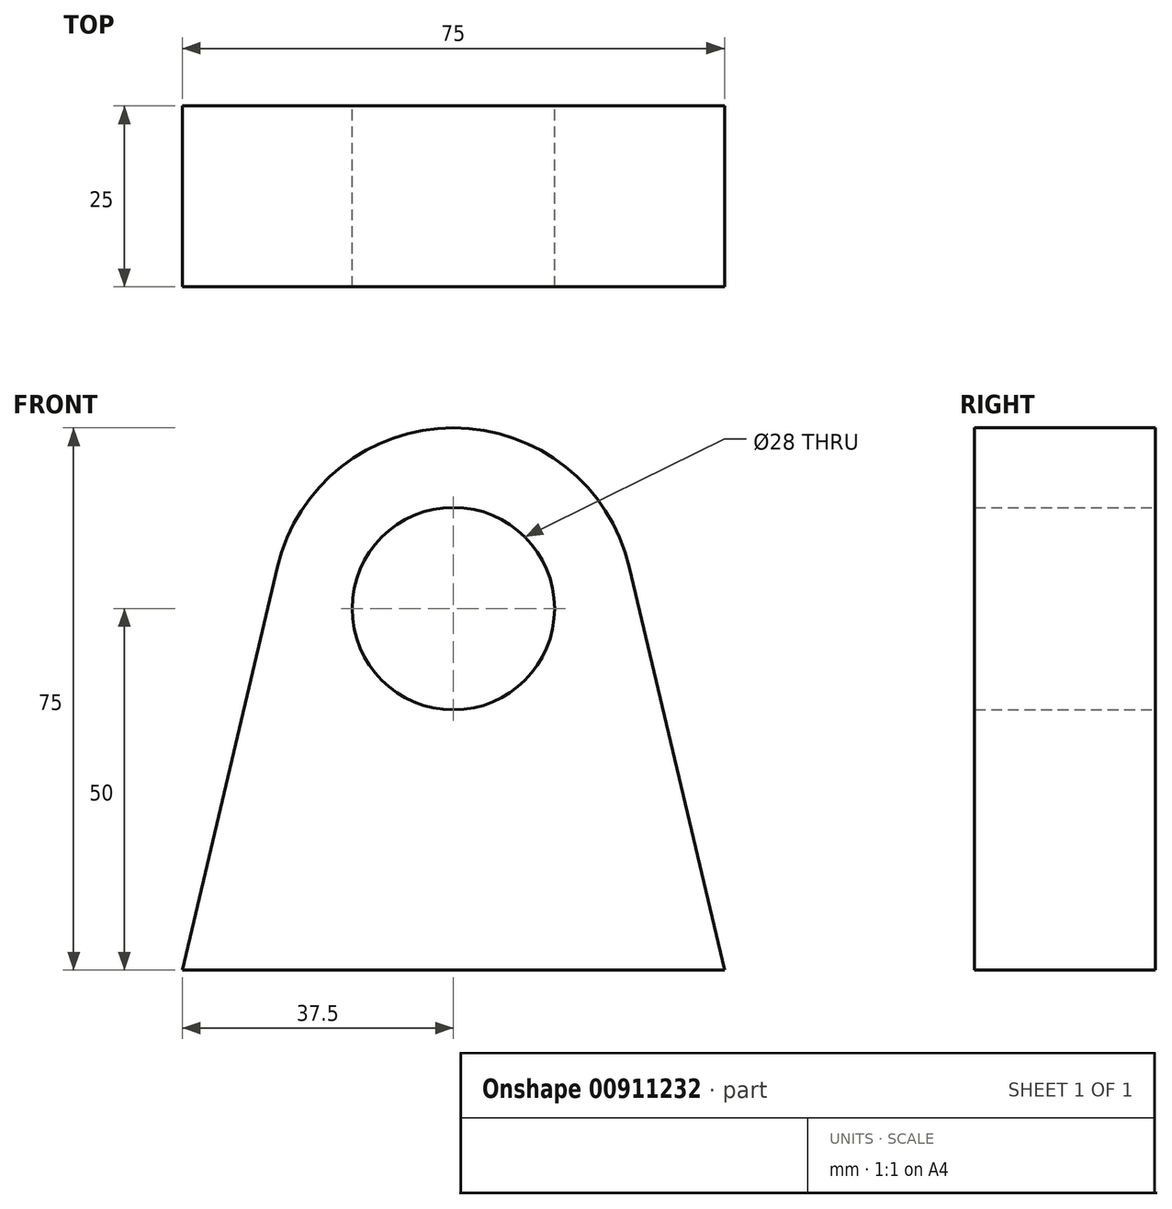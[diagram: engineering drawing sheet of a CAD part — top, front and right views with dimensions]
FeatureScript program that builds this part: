
annotation { "Feature Type Name" : "Feature", "Feature Type Description" : "" }
export const myFeature = defineFeature(function(context is Context, id is Id, definition is map)
    precondition{}
    {
        {
            var Q0;
            Q0=qCreatedBy(makeId("Front.planeOp"),FACE);
            var sketch = newSketch(context, id + "F0", { "sketchPlane" : qUnion([Q0])});
            skCircle(sketch, "E0", {"center": v(0, 50) * mm, "radius": 14 * mm});
            skArc(sketch, "E1", {"start": v(24.33, 55.75) * mm, "mid": v(0, 75) * mm, "end": v(-24.33, 55.75) * mm});
            skLineSegment(sketch, "E2", {"start": v(-37.5, 0) * mm, "end": v(37.5, 0) * mm});
            skLineSegment(sketch, "E3", {"start": v(37.5, 0) * mm, "end": v(24.33, 55.75) * mm});
            skLineSegment(sketch, "E4", {"start": v(-37.5, 0) * mm, "end": v(-24.33, 55.75) * mm});
            skSolve(sketch);
        }
        {
            var Q0;
            Q0=makeQuery(id+"F0.imprint","IMPRINT",FACE,{"disambiguationData":[TD([[makeQuery(id+"F0.imprint","IMPRINT",EDGE,{"derivedFrom":sQuery(id+"F0.wireOp",EDGE,"E0")}),-1.0]])]});
            extrude(context, id + "F1", {"entities" : qUnion([Q0]), "depth" : 25 * mm, "offsetDistance" : 25 * mm});
        }
    });
